# Revit family: LV NARI
name_source: partatom
category: Aparatos sanitarios
units: mm (PartAtom-declared; Revit-internal decimal feet)

## family parameters
Activar corte en vistas = No
Compartido = No
Corte con vacíos al cargar = No
Cota de conector redondo = Usar diámetro
Mantener orientación de anotación = No
Número OmniClass = 23.45.00.00
Punto de cálculo de habitación = No
Se basa en plano de trabajo = No
Siempre vertical = Sí
Tipo de pieza = Normal
Título OmniClass = Sanitary, Laundry, and Cleaning Equipment

## types (2) — shared parameters
Comentarios de tipo = SANIVEX
Fabricante = HELVEX

## per-type parameters (varying)
| type | Altura | Anchura | Descripción | Elevación por defecto | Features | Imagen de tipo | Instalación | Material | Profundidad | URL |
| LV CASSINI | 17" | 17" | Cassini Lavatory to Cap Without Sprill Way | 0" | Perfect Assembly; Uniformity | <Ninguno> |  |  | 7" | https://www.helvex.com.mx |
| LV NARI | 5" | 24" | Lavabo de Sobreponer sin Rebosadero. | 28" | Lavabo de sobreponer. Lavabo rectangular. Sin rebosadero. | LV NARI.png | De sobreponer. | Cerámica de alto brillo. Acabado duradero y resistente a las rayaduras. | 16" |  |

note: column(s) folded — value = type name in every type: Modelo

## geometry (parser evidence)
native form markers: Sweep x3
no freeform markers — native parametric forms only
